# Revit family: QF_MACOM_CA92C-N_G
name_source: partatom
category: Equipamento especial
units: mm (PartAtom-declared; Revit-internal decimal feet)

## family parameters
Com base no plano de trabalho = Não
Compartilhado = Não
Corte com vazios quando carregada = Não
Cota do conector redondo = Utilizar diâmetro
Número OmniClass = 23.40.40.14.17.11
Ponto de cálculo do ambiente = Não
Sempre na vertical = Sim
Tipo de parte = Normal
Título OmniClass = Cookers, Ovens, Stoves

## types (2) — shared parameters
Capacity in Liters = 180,0 L
Cycle = 60 Hz
Depth = 1142 mm
Descrição = CALDEIRÃO A GÁS MACOM
Elec Connection Height = 266 mm
Electric power = 100 W
Elevação padrão = 0 mm
Fabricante = MACOM
Gas Connection Height = 266 mm
Gas Pressure = 0,0 bar
Gas Size = 1"
Height = 1136 mm
Phase = 2
Show Clearances = Sim
URL = https://www.acosmacom.com.br
Volts = 220 V
Volume = 1,18 m³
Water Connection Height = 681 mm
Water Size = 1"
Weight = 247,00 kg
Width = 906 mm

## per-type parameters (varying)
| type | Gas Consumption GLP | Gas Consumption GN | Gas Input GLP | Gas Input GN |
| CA92C-N |  | 2,2 m³/h | 0 Btu/h | 20665 Kcal/h |
| CA92C-G | 1,80 Kg/h | 0,0 m³/h | 82000 Btu/h |  |

note: column(s) folded — value = type name in every type: Modelo

## geometry (parser evidence)
native form markers: Sweep x13
no freeform markers — native parametric forms only
